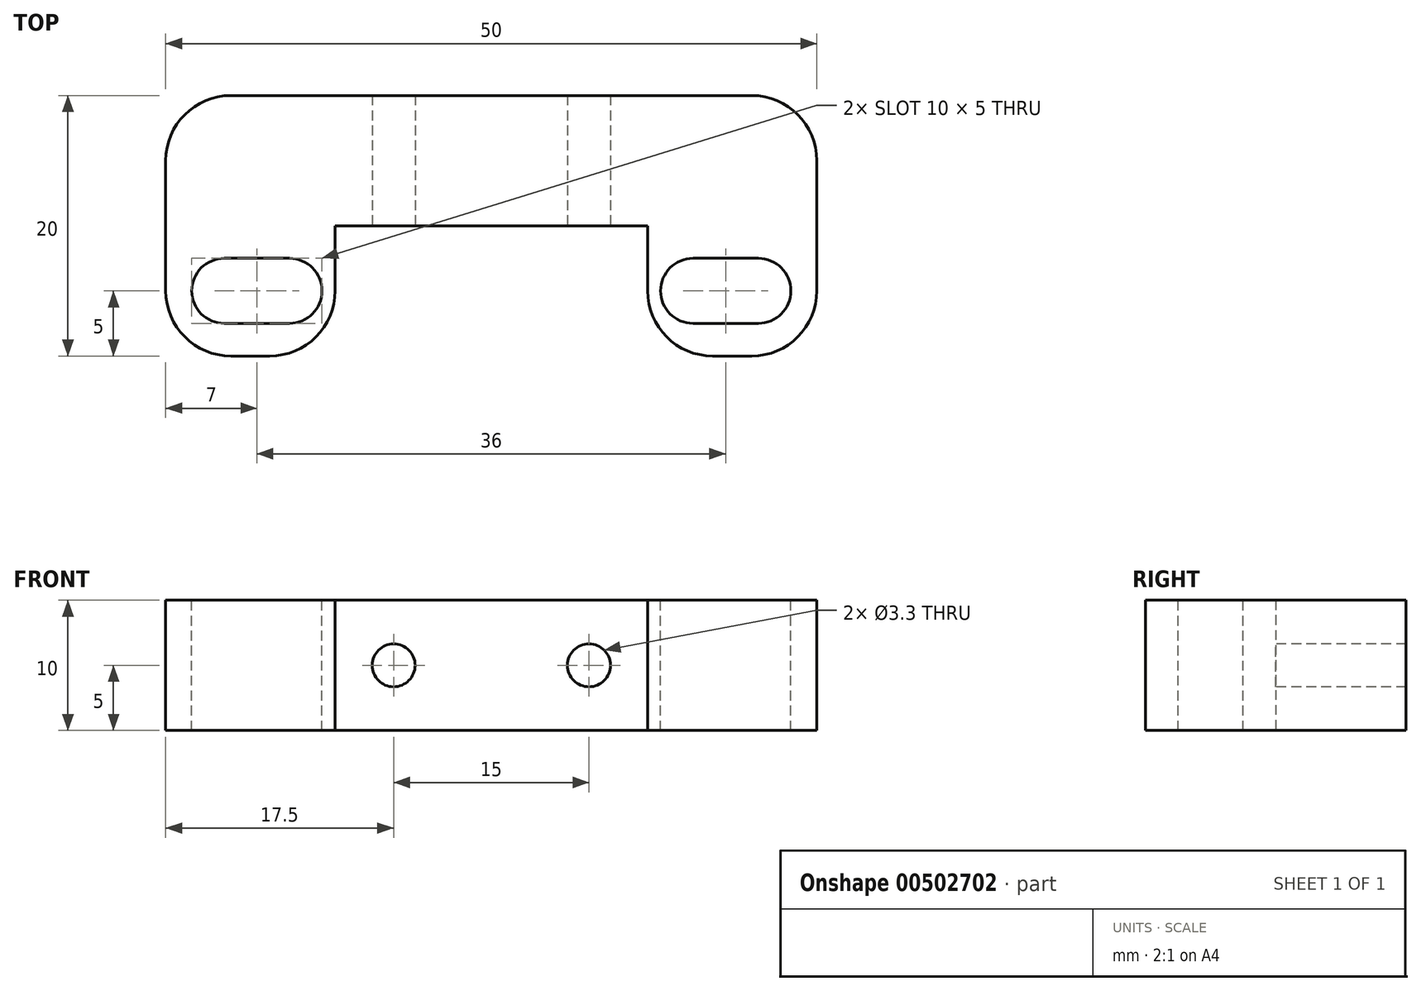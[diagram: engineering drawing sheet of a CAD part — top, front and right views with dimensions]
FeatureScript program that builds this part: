
annotation { "Feature Type Name" : "Feature", "Feature Type Description" : "" }
export const myFeature = defineFeature(function(context is Context, id is Id, definition is map)
    precondition{}
    {
        {
            var Q0;
            Q0=qCreatedBy(makeId("Top.planeOp"),FACE);
            var sketch = newSketch(context, id + "F0", { "sketchPlane" : qUnion([Q0])});
            skLineSegment(sketch, "E0.bottom", {"start": v(-25, 10) * mm, "end": v(25, 10) * mm});
            skLineSegment(sketch, "E0.top", {"start": v(-25, -10) * mm, "end": v(-12, -10) * mm});
            skLineSegment(sketch, "E0.left", {"start": v(-25, 10) * mm, "end": v(-25, -10) * mm});
            skLineSegment(sketch, "E0.right", {"start": v(25, 10) * mm, "end": v(25, -10) * mm});
            skLineSegment(sketch, "E1", {"start": v(-12, -10) * mm, "end": v(-12, 0) * mm});
            skLineSegment(sketch, "E2", {"start": v(-12, 0) * mm, "end": v(12, 0) * mm});
            skLineSegment(sketch, "E3", {"start": v(12, 0) * mm, "end": v(12, -10) * mm});
            skLineSegment(sketch, "E4.trimOffspring", {"start": v(12, -10) * mm, "end": v(25, -10) * mm});
            skSolve(sketch);
        }
        {
            var Q0;
            Q0=makeQuery(id+"F0.imprint","IMPRINT",FACE,{"disambiguationData":[TD([[makeQuery(id+"F0.imprint","IMPRINT",EDGE,{"derivedFrom":sQuery(id+"F0.wireOp",EDGE,"E0.bottom")}),-1.0]])]});
            extrude(context, id + "F1", {"entities" : qUnion([Q0]), "depth" : 10 * mm});
        }
        {
            var Q0;
            Q0=makeQuery(id+"F1.opExtrude","CAP_FACE",FACE,{"disambiguationData":[OSD([sQuery(id+"F0.wireOp",EDGE,"E0.bottom"),sQuery(id+"F0.wireOp",EDGE,"E0.top"),sQuery(id+"F0.wireOp",EDGE,"E0.left"),sQuery(id+"F0.wireOp",EDGE,"E0.right"),sQuery(id+"F0.wireOp",EDGE,"E1"),sQuery(id+"F0.wireOp",EDGE,"E2"),sQuery(id+"F0.wireOp",EDGE,"E3"),sQuery(id+"F0.wireOp",EDGE,"E4.trimOffspring")])],"isStart":false});
            var sketch = newSketch(context, id + "F2", { "sketchPlane" : qUnion([Q0])});
            skLineSegment(sketch, "E5", {"start": v(-18, -5) * mm, "end": v(18, -5) * mm, "construction": true});
            skLineSegment(sketch, "E6.bottom", {"start": v(-20.5, -2.5) * mm, "end": v(-15.5, -2.5) * mm});
            skLineSegment(sketch, "E6.top", {"start": v(-20.5, -7.5) * mm, "end": v(-15.5, -7.5) * mm});
            skLineSegment(sketch, "E6.left", {"start": v(-20.5, -2.5) * mm, "end": v(-20.5, -7.5) * mm});
            skLineSegment(sketch, "E6.right", {"start": v(-15.5, -2.5) * mm, "end": v(-15.5, -7.5) * mm});
            skLineSegment(sketch, "E7.bottom", {"start": v(15.5, -2.5) * mm, "end": v(20.5, -2.5) * mm});
            skLineSegment(sketch, "E7.top", {"start": v(15.5, -7.5) * mm, "end": v(20.5, -7.5) * mm});
            skLineSegment(sketch, "E7.left", {"start": v(15.5, -2.5) * mm, "end": v(15.5, -7.5) * mm});
            skLineSegment(sketch, "E7.right", {"start": v(20.5, -2.5) * mm, "end": v(20.5, -7.5) * mm});
            skArc(sketch, "E8", {"start": v(-20.5, -2.5) * mm, "mid": v(-23, -5) * mm, "end": v(-20.5, -7.5) * mm});
            skArc(sketch, "E9", {"start": v(-15.5, -7.5) * mm, "mid": v(-13, -5) * mm, "end": v(-15.5, -2.5) * mm});
            skArc(sketch, "E10", {"start": v(15.5, -2.5) * mm, "mid": v(13, -5) * mm, "end": v(15.5, -7.5) * mm});
            skArc(sketch, "E11", {"start": v(20.5, -7.5) * mm, "mid": v(23, -5) * mm, "end": v(20.5, -2.5) * mm});
            skSolve(sketch);
        }
        {
            var Q0;
            Q0 = qSketchRegion(id + "F2", true);
            extrude(context, id + "F3", {"entities" : qUnion([Q0]), "operationType" : NewBodyOperationType.REMOVE, "oppositeDirection" : true, "depth" : 10 * mm});
        }
        {
            var Q0;
            Q0=makeQuery(id+"F1.opExtrude","SWEPT_FACE",FACE,{"disambiguationData":[OSD([sQuery(id+"F0.wireOp",EDGE,"E2")])]});
            var sketch = newSketch(context, id + "F4", { "sketchPlane" : qUnion([Q0])});
            skLineSegment(sketch, "E12", {"start": v(-7.5, 5) * mm, "end": v(7.5, 5) * mm, "construction": true});
            skCircle(sketch, "E13", {"center": v(-7.5, 5) * mm, "radius": 1.65 * mm});
            skCircle(sketch, "E14", {"center": v(7.5, 5) * mm, "radius": 1.65 * mm});
            skSolve(sketch);
        }
        {
            var Q0;
            Q0 = qSketchRegion(id + "F4", true);
            extrude(context, id + "F5", {"entities" : qUnion([Q0]), "operationType" : NewBodyOperationType.REMOVE, "endBound" : BoundingType.THROUGH_ALL, "oppositeDirection" : true, "depth" : 25 * mm});
        }
        {
            var Q0;
            Q0=makeQuery(id+"F1.opExtrude","SWEPT_EDGE",EDGE,{"disambiguationData":[OSD([sQuery(id+"F0.wireOp",EDGE,"E0.top"),sQuery(id+"F0.wireOp",EDGE,"E0.left")])]});
            var Q1;
            Q1=makeQuery(id+"F1.opExtrude","SWEPT_EDGE",EDGE,{"disambiguationData":[OSD([sQuery(id+"F0.wireOp",EDGE,"E0.top"),sQuery(id+"F0.wireOp",EDGE,"E1")])]});
            var Q2;
            Q2=makeQuery(id+"F1.opExtrude","SWEPT_EDGE",EDGE,{"disambiguationData":[OSD([sQuery(id+"F0.wireOp",EDGE,"E3"),sQuery(id+"F0.wireOp",EDGE,"E4.trimOffspring")])]});
            var Q3;
            Q3=makeQuery(id+"F1.opExtrude","SWEPT_EDGE",EDGE,{"disambiguationData":[OSD([sQuery(id+"F0.wireOp",EDGE,"E0.right"),sQuery(id+"F0.wireOp",EDGE,"E4.trimOffspring")])]});
            var Q4;
            Q4=makeQuery(id+"F1.opExtrude","SWEPT_EDGE",EDGE,{"disambiguationData":[OSD([sQuery(id+"F0.wireOp",EDGE,"E0.bottom"),sQuery(id+"F0.wireOp",EDGE,"E0.right")])]});
            var Q5;
            Q5=makeQuery(id+"F1.opExtrude","SWEPT_EDGE",EDGE,{"disambiguationData":[OSD([sQuery(id+"F0.wireOp",EDGE,"E0.bottom"),sQuery(id+"F0.wireOp",EDGE,"E0.left")])]});
            fillet(context, id + "F6", {"entities" : qUnion([Q0, Q1, Q2, Q3, Q4, Q5]), "radius" : 5 * mm, "tangentPropagation" : true, "allowEdgeOverflow" : false});
        }
    });
